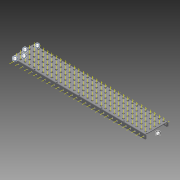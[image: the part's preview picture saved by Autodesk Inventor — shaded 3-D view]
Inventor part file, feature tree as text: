
AUTODESK INVENTOR PART (.ipt)
format: ipt  version: 2015 (Build 190159000, 159)  size: 2,834,432 bytes
history: native  units: in
note: dims shown in document units (in); Inventor stores cm internally (conversion verified against a paired STEP export)
features: other x216, pattern_linear x2, sheet_metal_op x1, extrude x1, imported_body x1, sketch x1
ambient origin geometry x8: Origin, YZ Plane, XZ Plane, XY Plane, X Axis, Y Axis, Z Axis, Center Point
bodies: Body1 (feature_tree)
feature tree (222):
  sheet_metal_op  "Fold1"
  other  "C-Channel"
  extrude  "length cut"  Depth=0.5in
  other  "top axis"
  other  "front axis"
  other  "back axis"
  pattern_linear  "top axes"  Spacing1=0.5in  [1 undecoded]
  pattern_linear  "horiz axes"  Spacing1=0.0in  [1 undecoded]
  other  "right plane"
  imported_body  "Base1"
  sketch  "Sketch1"  dims[d1=0.0in d4=0.5in d5=1.9685in d7=0.5in d10=0.5in d11=0.0in d12=0.0in d13=0.0in d14=-15.0in d15=0.0in d16=0.0in]
  other  "Work Point1"
  other  "Work Axis6"
  other  "Work Axis11"
  other  "Work Axis16"
  other  "Work Axis21"
  other  "Work Point2"
  other  "Work Point3"
  other  "Work Axis36"
  other  "Work Axis37"
  other  "Work Axis38"
  other  "Work Axis39"
  other  "Work Axis40"
  other  "Work Axis41"
  other  "Work Axis60"
  other  "Work Axis61"
  other  "Work Axis62"
  other  "Work Axis63"
  other  "Work Axis64"
  other  "Work Axis65"
  other  "Work Axis84"
  other  "Work Axis85"
  other  "Work Axis86"
  other  "Work Axis87"
  other  "Work Axis88"
  other  "Work Axis89"
  other  "Work Axis108"
  other  "Work Axis109"
  other  "Work Axis110"
  other  "Work Axis111"
  other  "Work Axis112"
  other  "Work Axis113"
  other  "Work Axis132"
  other  "Work Axis133"
  other  "Work Axis134"
  other  "Work Axis135"
  other  "Work Axis136"
  other  "Work Axis137"
  other  "Work Axis156"
  other  "Work Axis157"
  other  "Work Axis158"
  other  "Work Axis159"
  other  "Work Axis160"
  other  "Work Axis161"
  other  "Work Axis180"
  other  "Work Axis181"
  other  "Work Axis182"
  other  "Work Axis183"
  other  "Work Axis184"
  other  "Work Axis185"
  other  "Work Axis204"
  other  "Work Axis205"
  other  "Work Axis206"
  other  "Work Axis207"
  other  "Work Axis208"
  other  "Work Axis209"
  other  "Work Axis210"
  other  "Work Axis211"
  other  "Work Axis212"
  other  "Work Axis213"
  other  "Work Axis214"
  other  "Work Axis215"
  other  "Work Axis216"
  other  "Work Axis232"
  other  "Work Axis233"
  other  "Work Axis234"
  other  "Work Axis235"
  other  "Work Axis236"
  other  "Work Axis237"
  other  "Work Axis238"
  other  "Work Axis239"
  other  "Work Axis240"
  other  "Work Axis241"
  other  "Work Axis242"
  other  "Work Axis243"
  other  "Work Axis244"
  other  "Work Axis260"
  other  "Work Axis261"
  other  "Work Axis262"
  other  "Work Axis263"
  other  "Work Axis264"
  other  "Work Axis265"
  other  "Work Axis266"
  other  "Work Axis267"
  other  "Work Axis268"
  other  "Work Axis269"
  other  "Work Axis270"
  other  "Work Axis271"
  other  "Work Axis272"
  other  "Work Axis288"
  other  "Work Axis289"
  other  "Work Axis290"
  other  "Work Axis291"
  other  "Work Axis292"
  other  "Work Axis293"
  other  "Work Axis294"
  other  "Work Axis295"
  other  "Work Axis296"
  other  "Work Axis297"
  other  "Work Axis298"
  other  "Work Axis299"
  other  "Work Axis300"
  other  "Work Axis316"
  other  "Work Axis317"
  other  "Work Axis318"
  other  "Work Axis319"
  other  "Work Axis320"
  other  "Work Axis321"
  other  "Work Axis322"
  other  "Work Axis323"
  other  "Work Axis324"
  other  "Work Axis325"
  other  "Work Axis326"
  other  "Work Axis327"
  other  "Work Axis328"
  other  "Work Axis344"
  other  "Work Axis345"
  other  "Work Axis346"
  other  "Work Axis347"
  other  "Work Axis348"
  other  "Work Axis349"
  other  "Work Axis350"
  other  "Work Axis351"
  other  "Work Axis352"
  other  "Work Axis353"
  other  "Work Axis354"
  other  "Work Axis355"
  other  "Work Axis356"
  other  "Work Axis372"
  other  "Work Axis373"
  other  "Work Axis374"
  other  "Work Axis375"
  other  "Work Axis376"
  other  "Work Axis377"
  other  "Work Axis378"
  other  "Work Axis379"
  other  "Work Axis380"
  other  "Work Axis381"
  other  "Work Axis382"
  other  "Work Axis383"
  other  "Work Axis384"
  other  "left plane"
  other  "Work Axis400"
  other  "Work Axis401"
  other  "Work Axis402"
  other  "Work Axis403"
  other  "Work Axis404"
  other  "Work Axis405"
  other  "Work Axis406"
  other  "Work Axis407"
  other  "Work Axis408"
  other  "Work Axis409"
  other  "Work Axis410"
  other  "Work Axis411"
  other  "Work Axis412"
  other  "Work Axis413"
  other  "Work Axis414"
  other  "Work Axis415"
  other  "Work Axis416"
  other  "Work Axis417"
  other  "Work Axis418"
  other  "Work Axis419"
  other  "Work Axis420"
  other  "Work Axis421"
  other  "Work Axis422"
  other  "Work Axis423"
  other  "Work Axis424"
  other  "Work Axis425"
  other  "Work Axis426"
  other  "Work Axis427"
  other  "Work Axis428"
  other  "Work Axis429"
  other  "Work Axis430"
  other  "Work Axis431"
  other  "Work Axis432"
  other  "Work Axis433"
  other  "Work Axis434"
  other  "Work Axis435"
  other  "Work Axis436"
  other  "Work Axis437"
  other  "Work Axis438"
  other  "Work Axis439"
  other  "Work Axis440"
  other  "Work Axis441"
  other  "Work Axis442"
  other  "Work Axis443"
  other  "Work Axis444"
  other  "Work Axis445"
  other  "Work Axis446"
  other  "Work Axis447"
  other  "Work Axis448"
  other  "Work Axis449"
  other  "Work Axis450"
  other  "Work Axis451"
  other  "Work Axis452"
  other  "Work Axis453"
  other  "Work Axis454"
  other  "Work Axis455"
  other  "Work Axis456"
  other  "Work Axis457"
  other  "Work Axis458"
  other  "Work Axis459"
  other  "Work Axis460"
  other  "Work Axis461"
  other  "Work Axis462"
  other  "Work Axis463"
  other  "Work Axis464"
  other  "Work Axis465"
  other  "Work Axis466"
  other  "Work Axis467"
  other  "Work Axis468"
  other  "Work Axis469"
note: 2 required parameter values undecoded (feature->parameter linkage not recoverable at this tier; creation-order binding heuristic only, values carry confidence <= 0.55)
